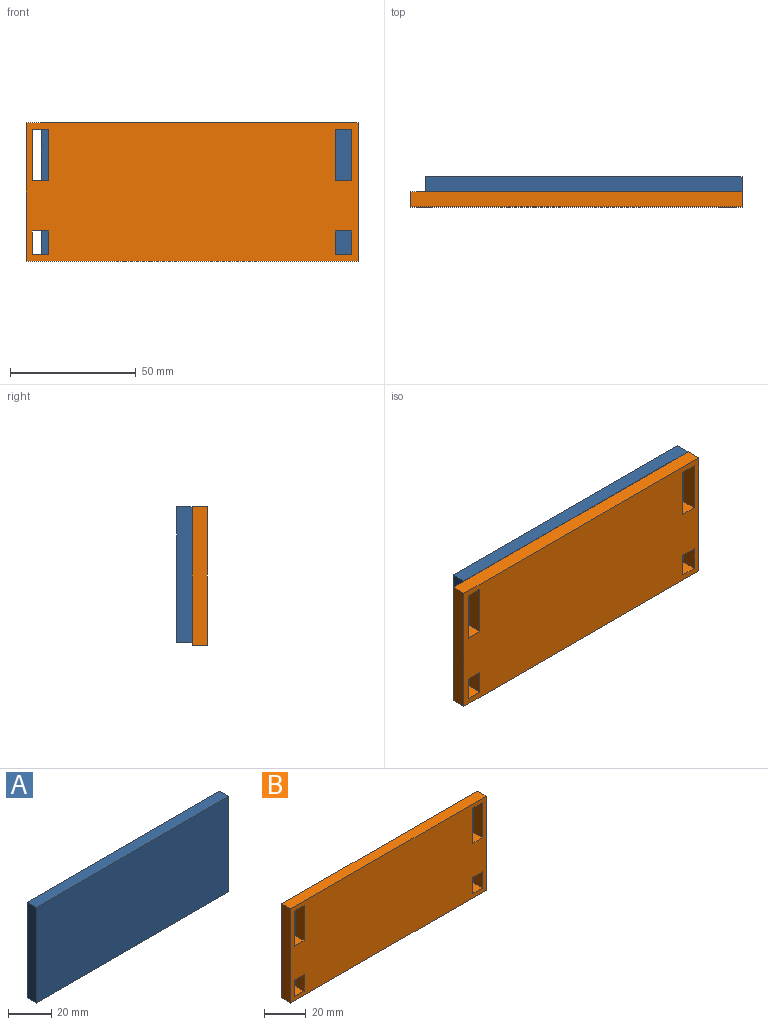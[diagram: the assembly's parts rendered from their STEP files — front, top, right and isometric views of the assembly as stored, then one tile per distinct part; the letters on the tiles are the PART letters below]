
ASSEMBLY  parts=2 mates=1
PART A: 6 faces, bbox 126x6x54 mm
  f0: plane 126x6mm, normal (0,0,-1), area 756mm2, adj f1,f3,f4,f5
  f1: plane 54x6mm, normal (1,0,0), area 324mm2, adj f0,f2,f4,f5
  f2: plane 126x6mm, normal (0,0,1), area 756mm2, adj f1,f3,f4,f5
  f3: plane 54x6mm, normal (-1,0,0), area 324mm2, adj f0,f2,f4,f5
  f4: plane 126x54mm, normal (0,-1,0), area 6804mm2, adj f0,f1,f2,f3
  f5: plane 126x54mm, normal (0,1,0), area 6804mm2, adj f0,f1,f2,f3
PART B: 22 faces, bbox 132x6x55 mm
  f0: plane 132x55mm, normal (0,-1,0), area 6870mm2, adj f2,f3,f4,f5,f6,f7,f8,f9
  f1: plane 132x55mm, normal (0,1,0), area 6870mm2, adj f2,f3,f4,f5,f6,f7,f8,f9
  f2: plane 132x6mm, normal (0,0,-1), area 792mm2, adj f0,f1,f3,f5
  f3: plane 55x6mm, normal (1,0,0), area 330mm2, adj f0,f1,f2,f4
  f4: plane 132x6mm, normal (0,0,1), area 792mm2, adj f0,f1,f3,f5
  f5: plane 55x6mm, normal (-1,0,0), area 330mm2, adj f0,f1,f2,f4
  f6: plane 6.5x6mm, normal (0,0,1), area 39mm2, adj f0,f1,f7,f9
  f7: plane 9.5x6mm, normal (-1,0,0), area 57mm2, adj f0,f1,f6,f8
  f8: plane 6.5x6mm, normal (0,0,-1), area 39mm2, adj f0,f1,f7,f9
  f9: plane 9.5x6mm, normal (1,0,0), area 57mm2, adj f0,f1,f6,f8
  f10: plane 20.5x6mm, normal (1,0,0), area 123mm2, adj f0,f1,f11,f13
  f11: plane 6.5x6mm, normal (0,0,1), area 39mm2, adj f0,f1,f10,f12
  f12: plane 20.5x6mm, normal (-1,0,0), area 123mm2, adj f0,f1,f11,f13
  f13: plane 6.5x6mm, normal (0,0,-1), area 39mm2, adj f0,f1,f10,f12
  f14: plane 9.5x6mm, normal (-1,0,0), area 57mm2, adj f0,f1,f15,f17
  f15: plane 6.5x6mm, normal (0,0,-1), area 39mm2, adj f0,f1,f14,f16
  f16: plane 9.5x6mm, normal (1,0,0), area 57mm2, adj f0,f1,f15,f17
  f17: plane 6.5x6mm, normal (0,0,1), area 39mm2, adj f0,f1,f14,f16
  f18: plane 20.5x6mm, normal (1,0,0), area 123mm2, adj f0,f1,f19,f21
  f19: plane 6.5x6mm, normal (0,0,1), area 39mm2, adj f0,f1,f18,f20
  f20: plane 20.5x6mm, normal (-1,0,0), area 123mm2, adj f0,f1,f19,f21
  f21: plane 6.5x6mm, normal (0,0,-1), area 39mm2, adj f0,f1,f18,f20
PLACE A t=(-2.93,-1.07,-3.57)mm
PLACE B t=(-5.93,-7.07,-4.07)mm
MATE fastened B.f1 <-> A.f4  axis (0,1,0) through (60.07,-7.07,23.43)mm
